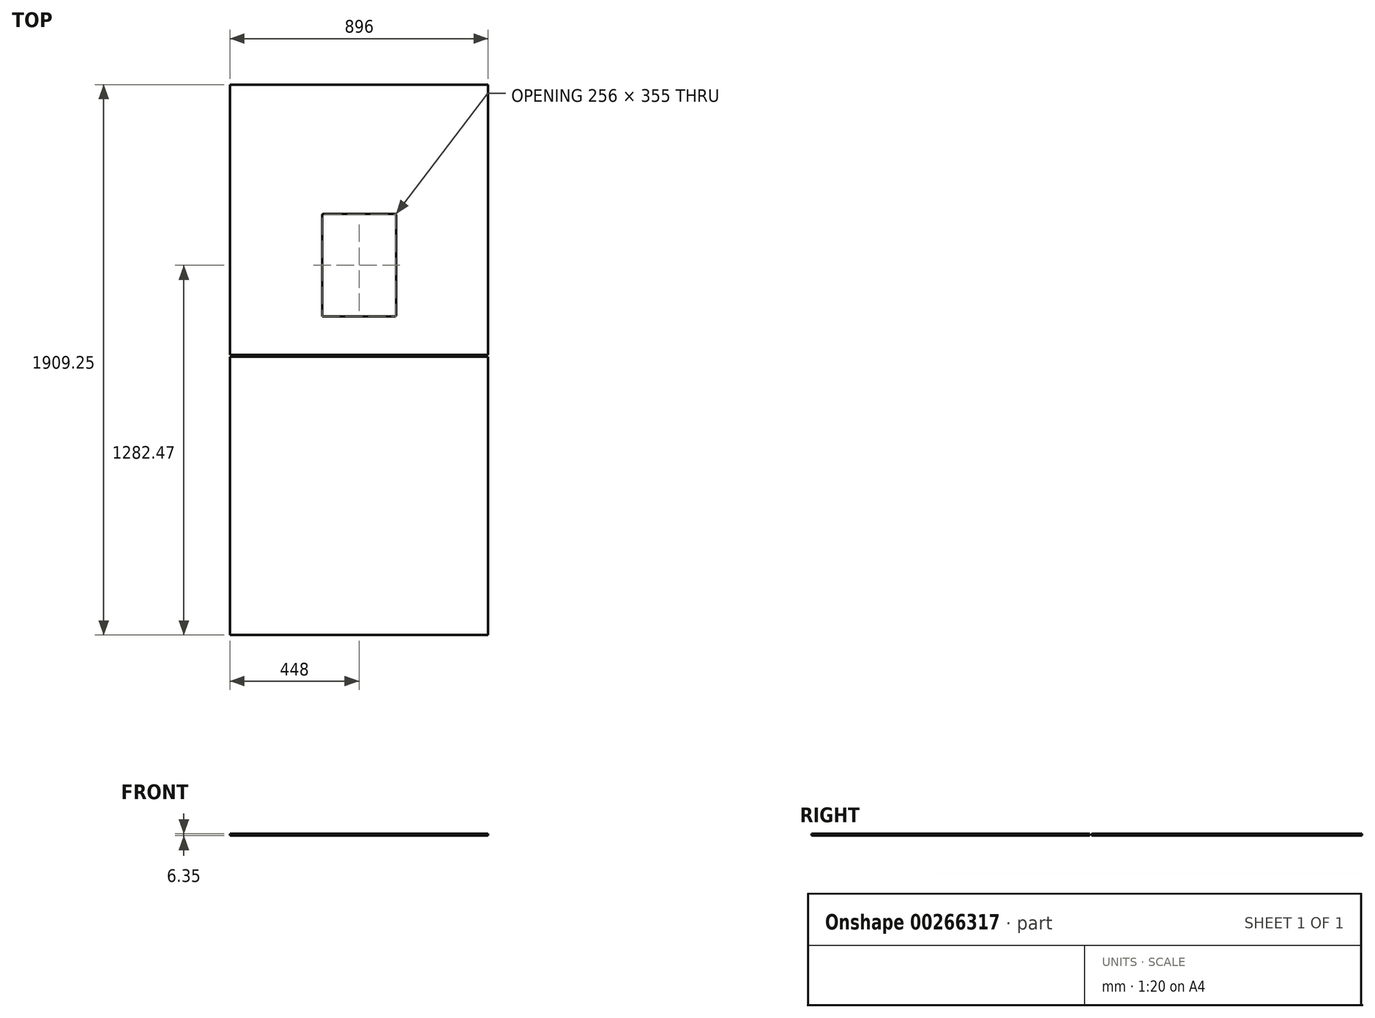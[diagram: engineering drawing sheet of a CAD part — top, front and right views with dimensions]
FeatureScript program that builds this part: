
annotation { "Feature Type Name" : "Feature", "Feature Type Description" : "" }
export const myFeature = defineFeature(function(context is Context, id is Id, definition is map)
    precondition{}
    {
        {
            var Q0;
            Q0=qCreatedBy(makeId("Top.planeOp"),FACE);
            var sketch = newSketch(context, id + "F0", { "sketchPlane" : qUnion([Q0])});
            skLineSegment(sketch, "E0.bottom", {"start": v(0, 0) * mm, "end": v(896, 0) * mm});
            skLineSegment(sketch, "E0.top", {"start": v(0, 1909.25) * mm, "end": v(896, 1909.25) * mm});
            skLineSegment(sketch, "E0.left", {"start": v(0, 0) * mm, "end": v(0, 1909.25) * mm});
            skLineSegment(sketch, "E0.right", {"start": v(896, 0) * mm, "end": v(896, 1909.25) * mm});
            skLineSegment(sketch, "E1.bottom", {"start": v(323, 1104.97) * mm, "end": v(573, 1104.97) * mm});
            skLineSegment(sketch, "E1.top", {"start": v(323, 1459.97) * mm, "end": v(573, 1459.97) * mm});
            skLineSegment(sketch, "E1.left", {"start": v(320, 1107.97) * mm, "end": v(320, 1456.97) * mm});
            skLineSegment(sketch, "E1.right", {"start": v(576, 1107.97) * mm, "end": v(576, 1456.97) * mm});
            skPoint(sketch, "E2.visualSharp", {"position": v(320, 1459.97) * mm});
            skArc(sketch, "E2.filletArc", {"start": v(323, 1459.97) * mm, "mid": v(320.88, 1459.1) * mm, "end": v(320, 1456.97) * mm});
            skPoint(sketch, "E3.visualSharp", {"position": v(576, 1459.97) * mm});
            skArc(sketch, "E3.filletArc", {"start": v(576, 1456.97) * mm, "mid": v(575.12, 1459.1) * mm, "end": v(573, 1459.97) * mm});
            skPoint(sketch, "E4.visualSharp", {"position": v(320, 1104.97) * mm});
            skArc(sketch, "E4.filletArc", {"start": v(320, 1107.97) * mm, "mid": v(320.88, 1105.85) * mm, "end": v(323, 1104.97) * mm});
            skPoint(sketch, "E5.visualSharp", {"position": v(576, 1104.97) * mm});
            skArc(sketch, "E5.filletArc", {"start": v(573, 1104.97) * mm, "mid": v(575.12, 1105.85) * mm, "end": v(576, 1107.97) * mm});
            skLineSegment(sketch, "E6", {"start": v(0, 965.25) * mm, "end": v(896, 965.25) * mm});
            skLineSegment(sketch, "E7", {"start": v(0, 971.75) * mm, "end": v(896, 971.75) * mm});
            skSolve(sketch);
        }
        {
            var Q0;
            Q0=makeQuery(id+"F0.imprint","IMPRINT",FACE,{"disambiguationData":[TD([[makeQuery(id+"F0.imprint","IMPRINT",EDGE,{"derivedFrom":sQuery(id+"F0.wireOp",EDGE,"E0.bottom")}),1.0]])]});
            extrude(context, id + "F1", {"entities" : qUnion([Q0]), "depth" : 6.35 * mm});
        }
        {
            var Q0;
            {var subQ0=sQuery(id+"F0.wireOp",EDGE,"E0.top");Q0=makeQuery(id+"F0.imprint","IMPRINT",FACE,{"disambiguationData":[TD([[makeQuery(id+"F0.imprint","IMPRINT",EDGE,{"derivedFrom":subQ0}),-1.0]])]});}
            extrude(context, id + "F2", {"entities" : qUnion([Q0]), "depth" : 6.35 * mm});
        }
    });
